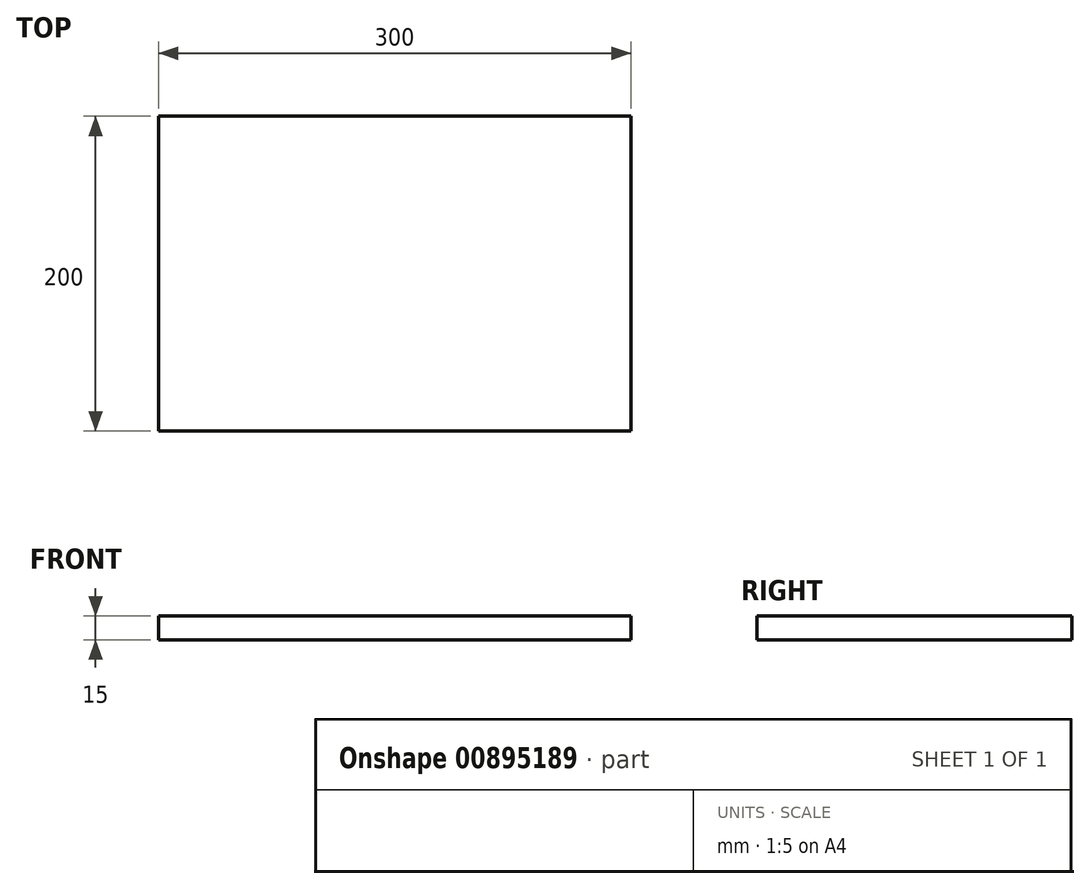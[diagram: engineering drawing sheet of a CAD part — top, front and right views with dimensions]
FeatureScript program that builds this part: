
annotation { "Feature Type Name" : "Feature", "Feature Type Description" : "" }
export const myFeature = defineFeature(function(context is Context, id is Id, definition is map)
    precondition{}
    {
        {
            var Q0;
            Q0=qCreatedBy(makeId("Top.planeOp"),FACE);
            var sketch = newSketch(context, id + "F0", { "sketchPlane" : qUnion([Q0])});
            skLineSegment(sketch, "E0.bottom", {"start": v(150, 100) * mm, "end": v(-150, 100) * mm});
            skLineSegment(sketch, "E0.top", {"start": v(150, -100) * mm, "end": v(-150, -100) * mm});
            skLineSegment(sketch, "E0.left", {"start": v(150, 100) * mm, "end": v(150, -100) * mm});
            skLineSegment(sketch, "E0.right", {"start": v(-150, 100) * mm, "end": v(-150, -100) * mm});
            skPoint(sketch, "E0.middle", {"position": v(0, 0) * mm});
            skSolve(sketch);
        }
        {
            var Q0;
            Q0 = qSketchRegion(id + "F0", true);
            extrude(context, id + "F1", {"entities" : qUnion([Q0]), "depth" : 15 * mm, "offsetDistance" : 25 * mm});
        }
    });
